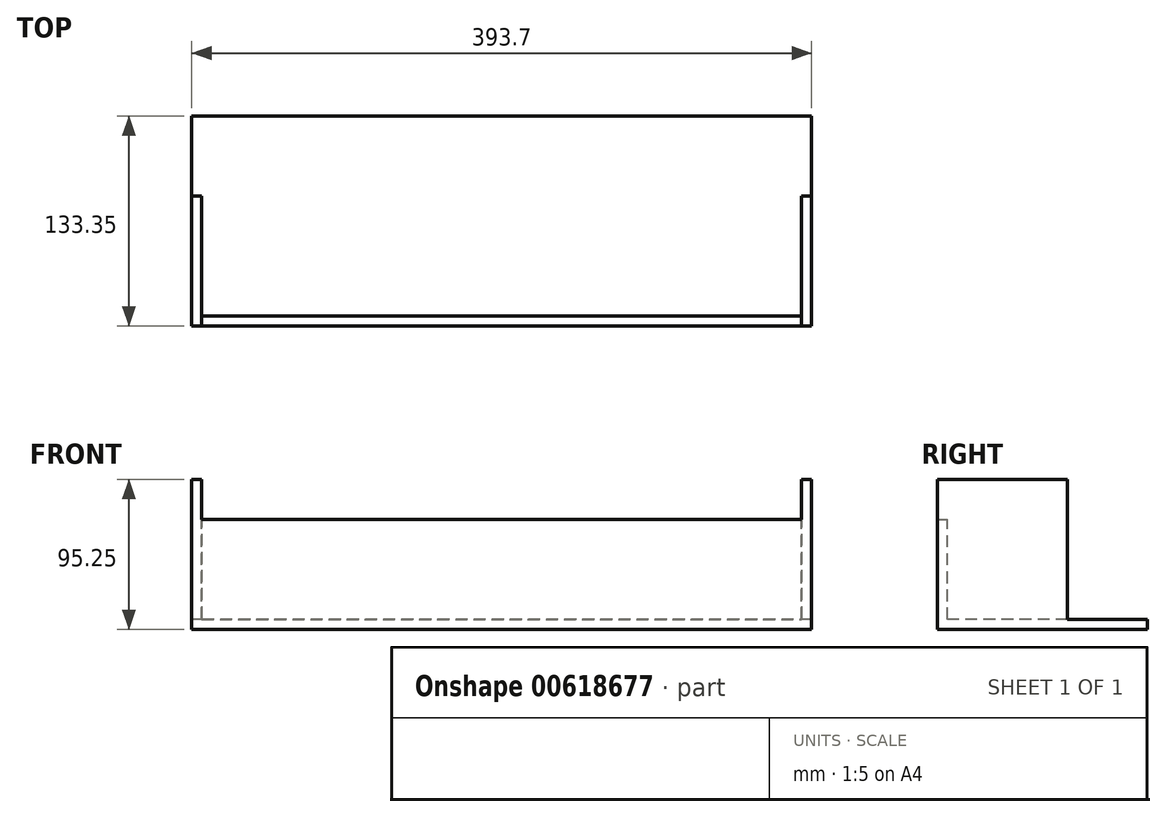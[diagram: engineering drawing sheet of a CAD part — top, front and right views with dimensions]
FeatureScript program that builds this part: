
annotation { "Feature Type Name" : "Feature", "Feature Type Description" : "" }
export const myFeature = defineFeature(function(context is Context, id is Id, definition is map)
    precondition{}
    {
        {
            var Q0;
            Q0=qCreatedBy(makeId("Front.planeOp"),FACE);
            var sketch = newSketch(context, id + "F0", { "sketchPlane" : qUnion([Q0])});
            skLineSegment(sketch, "E0.bottom", {"start": v(196.85, 47.63) * mm, "end": v(-196.85, 47.63) * mm});
            skLineSegment(sketch, "E0.top", {"start": v(196.85, -47.63) * mm, "end": v(-196.85, -47.63) * mm});
            skLineSegment(sketch, "E0.left", {"start": v(196.85, 47.63) * mm, "end": v(196.85, -47.63) * mm});
            skLineSegment(sketch, "E0.right", {"start": v(-196.85, 47.63) * mm, "end": v(-196.85, -47.63) * mm});
            skPoint(sketch, "E0.middle", {"position": v(0, 0) * mm});
            skSolve(sketch);
        }
        {
            var Q0;
            Q0=makeQuery(id+"F0.imprint","IMPRINT",FACE,{"disambiguationData":[TD([[makeQuery(id+"F0.imprint","IMPRINT",EDGE,{"derivedFrom":sQuery(id+"F0.wireOp",EDGE,"E0.bottom")}),1.0]])]});
            extrude(context, id + "F1", {"entities" : qUnion([Q0]), "depth" : 133.35 * mm, "offsetDistance" : 25.4 * mm});
        }
        {
            var Q0;
            Q0=makeQuery(id+"F1.opExtrude","SWEPT_FACE",FACE,{"disambiguationData":[OSD([sQuery(id+"F0.wireOp",EDGE,"E0.bottom")])]});
            var sketch = newSketch(context, id + "F2", { "sketchPlane" : qUnion([Q0])});
            skLineSegment(sketch, "E1.bottom", {"start": v(-190.5, 0) * mm, "end": v(190.5, 0) * mm});
            skLineSegment(sketch, "E1.top", {"start": v(-190.5, -127) * mm, "end": v(190.5, -127) * mm});
            skLineSegment(sketch, "E1.left", {"start": v(-190.5, 0) * mm, "end": v(-190.5, -127) * mm});
            skLineSegment(sketch, "E1.right", {"start": v(190.5, 0) * mm, "end": v(190.5, -127) * mm});
            skSolve(sketch);
        }
        {
            var Q0;
            Q0=makeQuery(id+"F2.imprint","IMPRINT",FACE,{"disambiguationData":[TD([[makeQuery(id+"F2.imprint","IMPRINT",EDGE,{"derivedFrom":sQuery(id+"F2.wireOp",EDGE,"E1.bottom")}),1.0]])]});
            extrude(context, id + "F3", {"entities" : qUnion([Q0]), "operationType" : NewBodyOperationType.REMOVE, "oppositeDirection" : true, "depth" : 88.9 * mm, "offsetDistance" : 25.4 * mm});
        }
        {
            var Q0;
            Q0=makeQuery(id+"F1.opExtrude","SWEPT_FACE",FACE,{"disambiguationData":[OSD([sQuery(id+"F0.wireOp",EDGE,"E0.right")])]});
            var sketch = newSketch(context, id + "F4", { "sketchPlane" : qUnion([Q0])});
            skLineSegment(sketch, "E2.bottom", {"start": v(0, 47.63) * mm, "end": v(50.8, 47.63) * mm});
            skLineSegment(sketch, "E2.top", {"start": v(0, -41.27) * mm, "end": v(50.8, -41.27) * mm});
            skLineSegment(sketch, "E2.left", {"start": v(0, 47.63) * mm, "end": v(0, -41.27) * mm});
            skLineSegment(sketch, "E2.right", {"start": v(50.8, 47.63) * mm, "end": v(50.8, -41.27) * mm});
            skSolve(sketch);
        }
        {
            var Q0;
            Q0=makeQuery(id+"F4.imprint","IMPRINT",FACE,{"disambiguationData":[TD([[makeQuery(id+"F4.imprint","IMPRINT",EDGE,{"derivedFrom":sQuery(id+"F4.wireOp",EDGE,"E2.bottom")}),1.0]])]});
            extrude(context, id + "F5", {"entities" : qUnion([Q0]), "operationType" : NewBodyOperationType.REMOVE, "oppositeDirection" : true, "depth" : 406.4 * mm, "offsetDistance" : 25.4 * mm});
        }
        {
            var Q0;
            Q0=makeQuery(id+"F3.boolean.opBoolean","COPY",FACE,{"derivedFrom":makeQuery(id+"F3.opExtrude","SWEPT_FACE",FACE,{"disambiguationData":[OSD([sQuery(id+"F2.wireOp",EDGE,"E1.top")])]})});
            var sketch = newSketch(context, id + "F6", { "sketchPlane" : qUnion([Q0])});
            skLineSegment(sketch, "E3.bottom", {"start": v(-190.5, 47.63) * mm, "end": v(190.5, 47.63) * mm});
            skLineSegment(sketch, "E3.top", {"start": v(-190.5, 22.23) * mm, "end": v(190.5, 22.23) * mm});
            skLineSegment(sketch, "E3.left", {"start": v(-190.5, 47.63) * mm, "end": v(-190.5, 22.23) * mm});
            skLineSegment(sketch, "E3.right", {"start": v(190.5, 47.63) * mm, "end": v(190.5, 22.23) * mm});
            skSolve(sketch);
        }
        {
            var Q0;
            Q0=makeQuery(id+"F6.imprint","IMPRINT",FACE,{"disambiguationData":[TD([[makeQuery(id+"F6.imprint","IMPRINT",EDGE,{"derivedFrom":sQuery(id+"F6.wireOp",EDGE,"E3.bottom")}),1.0]])]});
            extrude(context, id + "F7", {"entities" : qUnion([Q0]), "operationType" : NewBodyOperationType.REMOVE, "oppositeDirection" : true, "depth" : 25.4 * mm, "offsetDistance" : 25.4 * mm});
        }
    });
